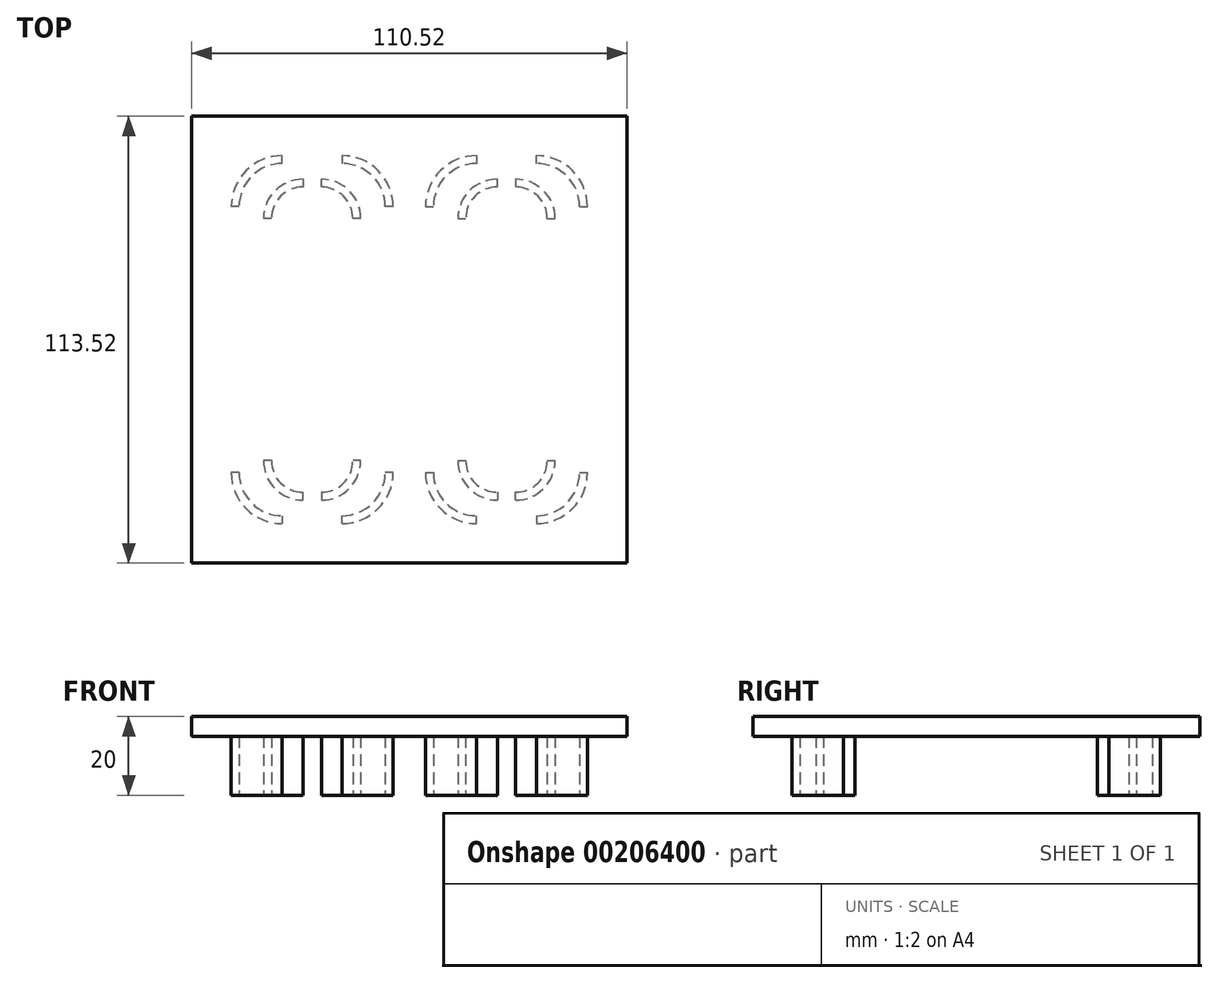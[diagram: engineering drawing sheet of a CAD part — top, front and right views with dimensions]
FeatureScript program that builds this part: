
annotation { "Feature Type Name" : "Feature", "Feature Type Description" : "" }
export const myFeature = defineFeature(function(context is Context, id is Id, definition is map)
    precondition{}
    {
        {
            var Q0;
            Q0=qCreatedBy(makeId("Top.planeOp"),FACE);
            var sketch = newSketch(context, id + "F0", { "sketchPlane" : qUnion([Q0])});
            skLineSegment(sketch, "E0", {"start": v(0, 27.76) * mm, "end": v(84.13, 27.76) * mm, "construction": true});
            skArc(sketch, "E1", {"start": v(22.34, 40.76) * mm, "mid": v(15.27, 37.83) * mm, "end": v(12.34, 30.76) * mm});
            skArc(sketch, "E2", {"start": v(37.03, 30.76) * mm, "mid": v(34.1, 37.83) * mm, "end": v(27.03, 40.76) * mm});
            skArc(sketch, "E3", {"start": v(45.26, 33.76) * mm, "mid": v(41.45, 42.95) * mm, "end": v(32.26, 46.76) * mm});
            skArc(sketch, "E4", {"start": v(17.11, 46.76) * mm, "mid": v(7.92, 42.95) * mm, "end": v(4.11, 33.76) * mm});
            skArc(sketch, "E5", {"start": v(6.11, 33.76) * mm, "mid": v(9.34, 41.54) * mm, "end": v(17.11, 44.76) * mm});
            skArc(sketch, "E6", {"start": v(43.26, 33.76) * mm, "mid": v(40.04, 41.54) * mm, "end": v(32.26, 44.76) * mm});
            skArc(sketch, "E7", {"start": v(14.34, 30.76) * mm, "mid": v(16.69, 36.42) * mm, "end": v(22.34, 38.76) * mm});
            skArc(sketch, "E8", {"start": v(27.03, 38.76) * mm, "mid": v(32.69, 36.42) * mm, "end": v(35.03, 30.76) * mm});
            skLineSegment(sketch, "E9", {"start": v(4.11, 33.76) * mm, "end": v(6.11, 33.76) * mm});
            skLineSegment(sketch, "E10", {"start": v(17.11, 46.76) * mm, "end": v(17.11, 44.76) * mm});
            skLineSegment(sketch, "E11", {"start": v(12.34, 30.76) * mm, "end": v(14.34, 30.76) * mm});
            skLineSegment(sketch, "E12", {"start": v(22.34, 38.76) * mm, "end": v(22.34, 40.76) * mm});
            skLineSegment(sketch, "E13", {"start": v(27.03, 40.76) * mm, "end": v(27.03, 38.76) * mm});
            skLineSegment(sketch, "E14", {"start": v(35.03, 30.76) * mm, "end": v(37.03, 30.76) * mm});
            skLineSegment(sketch, "E15", {"start": v(32.26, 44.76) * mm, "end": v(32.26, 46.76) * mm});
            skLineSegment(sketch, "E16", {"start": v(43.26, 33.76) * mm, "end": v(45.26, 33.76) * mm});
            skLineSegment(sketch, "E17.MirrorCS", {"start": v(4.11, -33.76) * mm, "end": v(6.11, -33.76) * mm});
            skArc(sketch, "E18.MirrorCS", {"start": v(17.11, -46.76) * mm, "mid": v(7.92, -42.95) * mm, "end": v(4.11, -33.76) * mm});
            skLineSegment(sketch, "E19.MirrorCS", {"start": v(17.11, -46.76) * mm, "end": v(17.11, -44.76) * mm});
            skArc(sketch, "E20.MirrorCS", {"start": v(6.11, -33.76) * mm, "mid": v(9.34, -41.54) * mm, "end": v(17.11, -44.76) * mm});
            skLineSegment(sketch, "E21.MirrorCS", {"start": v(12.34, -30.76) * mm, "end": v(14.34, -30.76) * mm});
            skArc(sketch, "E22.MirrorCS", {"start": v(22.34, -40.76) * mm, "mid": v(15.27, -37.83) * mm, "end": v(12.34, -30.76) * mm});
            skLineSegment(sketch, "E23.MirrorCS", {"start": v(22.34, -38.76) * mm, "end": v(22.34, -40.76) * mm});
            skArc(sketch, "E24.MirrorCS", {"start": v(14.34, -30.76) * mm, "mid": v(16.69, -36.42) * mm, "end": v(22.34, -38.76) * mm});
            skLineSegment(sketch, "E25.MirrorCS", {"start": v(27.03, -40.76) * mm, "end": v(27.03, -38.76) * mm});
            skArc(sketch, "E26.MirrorCS", {"start": v(37.03, -30.76) * mm, "mid": v(34.1, -37.83) * mm, "end": v(27.03, -40.76) * mm});
            skLineSegment(sketch, "E27.MirrorCS", {"start": v(35.03, -30.76) * mm, "end": v(37.03, -30.76) * mm});
            skArc(sketch, "E28.MirrorCS", {"start": v(27.03, -38.76) * mm, "mid": v(32.69, -36.42) * mm, "end": v(35.03, -30.76) * mm});
            skArc(sketch, "E29.MirrorCS", {"start": v(43.26, -33.76) * mm, "mid": v(40.04, -41.54) * mm, "end": v(32.26, -44.76) * mm});
            skLineSegment(sketch, "E30.MirrorCS", {"start": v(32.26, -44.76) * mm, "end": v(32.26, -46.76) * mm});
            skArc(sketch, "E31.MirrorCS", {"start": v(45.26, -33.76) * mm, "mid": v(41.45, -42.95) * mm, "end": v(32.26, -46.76) * mm});
            skLineSegment(sketch, "E32.MirrorCS", {"start": v(43.26, -33.76) * mm, "end": v(45.26, -33.76) * mm});
            skLineSegment(sketch, "E33.MirrorCS", {"start": v(-17.11, 46.76) * mm, "end": v(-17.11, 44.76) * mm});
            skArc(sketch, "E34.MirrorCS", {"start": v(-17.11, 46.76) * mm, "mid": v(-7.92, 42.95) * mm, "end": v(-4.11, 33.76) * mm});
            skLineSegment(sketch, "E35.MirrorCS", {"start": v(-4.11, 33.76) * mm, "end": v(-6.11, 33.76) * mm});
            skArc(sketch, "E36.MirrorCS", {"start": v(-6.11, 33.76) * mm, "mid": v(-9.34, 41.54) * mm, "end": v(-17.11, 44.76) * mm});
            skLineSegment(sketch, "E37.MirrorCS", {"start": v(-12.34, 30.76) * mm, "end": v(-14.34, 30.76) * mm});
            skArc(sketch, "E38.MirrorCS", {"start": v(-22.34, 40.76) * mm, "mid": v(-15.27, 37.83) * mm, "end": v(-12.34, 30.76) * mm});
            skLineSegment(sketch, "E39.MirrorCS", {"start": v(-22.34, 38.76) * mm, "end": v(-22.34, 40.76) * mm});
            skArc(sketch, "E40.MirrorCS", {"start": v(-14.34, 30.76) * mm, "mid": v(-16.69, 36.42) * mm, "end": v(-22.34, 38.76) * mm});
            skLineSegment(sketch, "E41.MirrorCS", {"start": v(-27.03, 40.76) * mm, "end": v(-27.03, 38.76) * mm});
            skArc(sketch, "E42.MirrorCS", {"start": v(-37.03, 30.76) * mm, "mid": v(-34.1, 37.83) * mm, "end": v(-27.03, 40.76) * mm});
            skLineSegment(sketch, "E43.MirrorCS", {"start": v(-35.03, 30.76) * mm, "end": v(-37.03, 30.76) * mm});
            skArc(sketch, "E44.MirrorCS", {"start": v(-27.03, 38.76) * mm, "mid": v(-32.69, 36.42) * mm, "end": v(-35.03, 30.76) * mm});
            skLineSegment(sketch, "E45.MirrorCS", {"start": v(-32.26, 44.76) * mm, "end": v(-32.26, 46.76) * mm});
            skArc(sketch, "E46.MirrorCS", {"start": v(-45.26, 33.76) * mm, "mid": v(-41.45, 42.95) * mm, "end": v(-32.26, 46.76) * mm});
            skLineSegment(sketch, "E47.MirrorCS", {"start": v(-43.26, 33.76) * mm, "end": v(-45.26, 33.76) * mm});
            skArc(sketch, "E48.MirrorCS", {"start": v(-43.26, 33.76) * mm, "mid": v(-40.04, 41.54) * mm, "end": v(-32.26, 44.76) * mm});
            skLineSegment(sketch, "E49.MirrorCS", {"start": v(-4.11, -33.76) * mm, "end": v(-6.11, -33.76) * mm});
            skArc(sketch, "E50.MirrorCS", {"start": v(-17.11, -46.76) * mm, "mid": v(-7.92, -42.95) * mm, "end": v(-4.11, -33.76) * mm});
            skLineSegment(sketch, "E51.MirrorCS", {"start": v(-17.11, -46.76) * mm, "end": v(-17.11, -44.76) * mm});
            skArc(sketch, "E52.MirrorCS", {"start": v(-6.11, -33.76) * mm, "mid": v(-9.34, -41.54) * mm, "end": v(-17.11, -44.76) * mm});
            skArc(sketch, "E53.MirrorCS", {"start": v(-22.34, -40.76) * mm, "mid": v(-15.27, -37.83) * mm, "end": v(-12.34, -30.76) * mm});
            skLineSegment(sketch, "E54.MirrorCS", {"start": v(-22.34, -38.76) * mm, "end": v(-22.34, -40.76) * mm});
            skArc(sketch, "E55.MirrorCS", {"start": v(-14.34, -30.76) * mm, "mid": v(-16.69, -36.42) * mm, "end": v(-22.34, -38.76) * mm});
            skLineSegment(sketch, "E56.MirrorCS", {"start": v(-12.34, -30.76) * mm, "end": v(-14.34, -30.76) * mm});
            skLineSegment(sketch, "E57.MirrorCS", {"start": v(-27.03, -40.76) * mm, "end": v(-27.03, -38.76) * mm});
            skArc(sketch, "E58.MirrorCS", {"start": v(-37.03, -30.76) * mm, "mid": v(-34.1, -37.83) * mm, "end": v(-27.03, -40.76) * mm});
            skLineSegment(sketch, "E59.MirrorCS", {"start": v(-35.03, -30.76) * mm, "end": v(-37.03, -30.76) * mm});
            skArc(sketch, "E60.MirrorCS", {"start": v(-27.03, -38.76) * mm, "mid": v(-32.69, -36.42) * mm, "end": v(-35.03, -30.76) * mm});
            skLineSegment(sketch, "E61.MirrorCS", {"start": v(-32.26, -44.76) * mm, "end": v(-32.26, -46.76) * mm});
            skArc(sketch, "E62.MirrorCS", {"start": v(-45.26, -33.76) * mm, "mid": v(-41.45, -42.95) * mm, "end": v(-32.26, -46.76) * mm});
            skLineSegment(sketch, "E63.MirrorCS", {"start": v(-43.26, -33.76) * mm, "end": v(-45.26, -33.76) * mm});
            skArc(sketch, "E64.MirrorCS", {"start": v(-43.26, -33.76) * mm, "mid": v(-40.04, -41.54) * mm, "end": v(-32.26, -44.76) * mm});
            skSolve(sketch);
        }
        {
            var Q0;
            Q0 = qSketchRegion(id + "F0", true);
            extrude(context, id + "F1", {"entities" : qUnion([Q0]), "depth" : 15 * mm});
        }
        {
            var Q0;
            Q0=makeQuery(id+"F1.opExtrude","CAP_FACE",FACE,{"disambiguationData":[OSD([sQuery(id+"F0.wireOp",EDGE,"E45.MirrorCS"),sQuery(id+"F0.wireOp",EDGE,"E46.MirrorCS"),sQuery(id+"F0.wireOp",EDGE,"E47.MirrorCS"),sQuery(id+"F0.wireOp",EDGE,"E48.MirrorCS")])],"isStart":false});
            var sketch = newSketch(context, id + "F2", { "sketchPlane" : qUnion([Q0])});
            skLineSegment(sketch, "E65", {"start": v(55.26, 56.76) * mm, "end": v(55.26, 0) * mm});
            skLineSegment(sketch, "E66", {"start": v(55.26, 56.76) * mm, "end": v(0, 56.76) * mm});
            skLineSegment(sketch, "E67", {"start": v(0, 0) * mm, "end": v(0, 7.33) * mm, "construction": true});
            skLineSegment(sketch, "E68", {"start": v(0, 0) * mm, "end": v(7.25, 0) * mm, "construction": true});
            skLineSegment(sketch, "E69.MirrorCS", {"start": v(-55.26, 56.76) * mm, "end": v(0, 56.76) * mm});
            skLineSegment(sketch, "E70.MirrorCS", {"start": v(-55.26, 56.76) * mm, "end": v(-55.26, 0) * mm});
            skLineSegment(sketch, "E71.MirrorCS", {"start": v(-55.26, -56.76) * mm, "end": v(-55.26, 0) * mm});
            skLineSegment(sketch, "E72.MirrorCS", {"start": v(-55.26, -56.76) * mm, "end": v(0, -56.76) * mm});
            skLineSegment(sketch, "E73.MirrorCS", {"start": v(55.26, -56.76) * mm, "end": v(0, -56.76) * mm});
            skLineSegment(sketch, "E74.MirrorCS", {"start": v(55.26, -56.76) * mm, "end": v(55.26, 0) * mm});
            skSolve(sketch);
        }
        {
            var Q0;
            Q0 = qSketchRegion(id + "F2", true);
            extrude(context, id + "F3", {"entities" : qUnion([Q0]), "depth" : 5 * mm});
        }
    });
